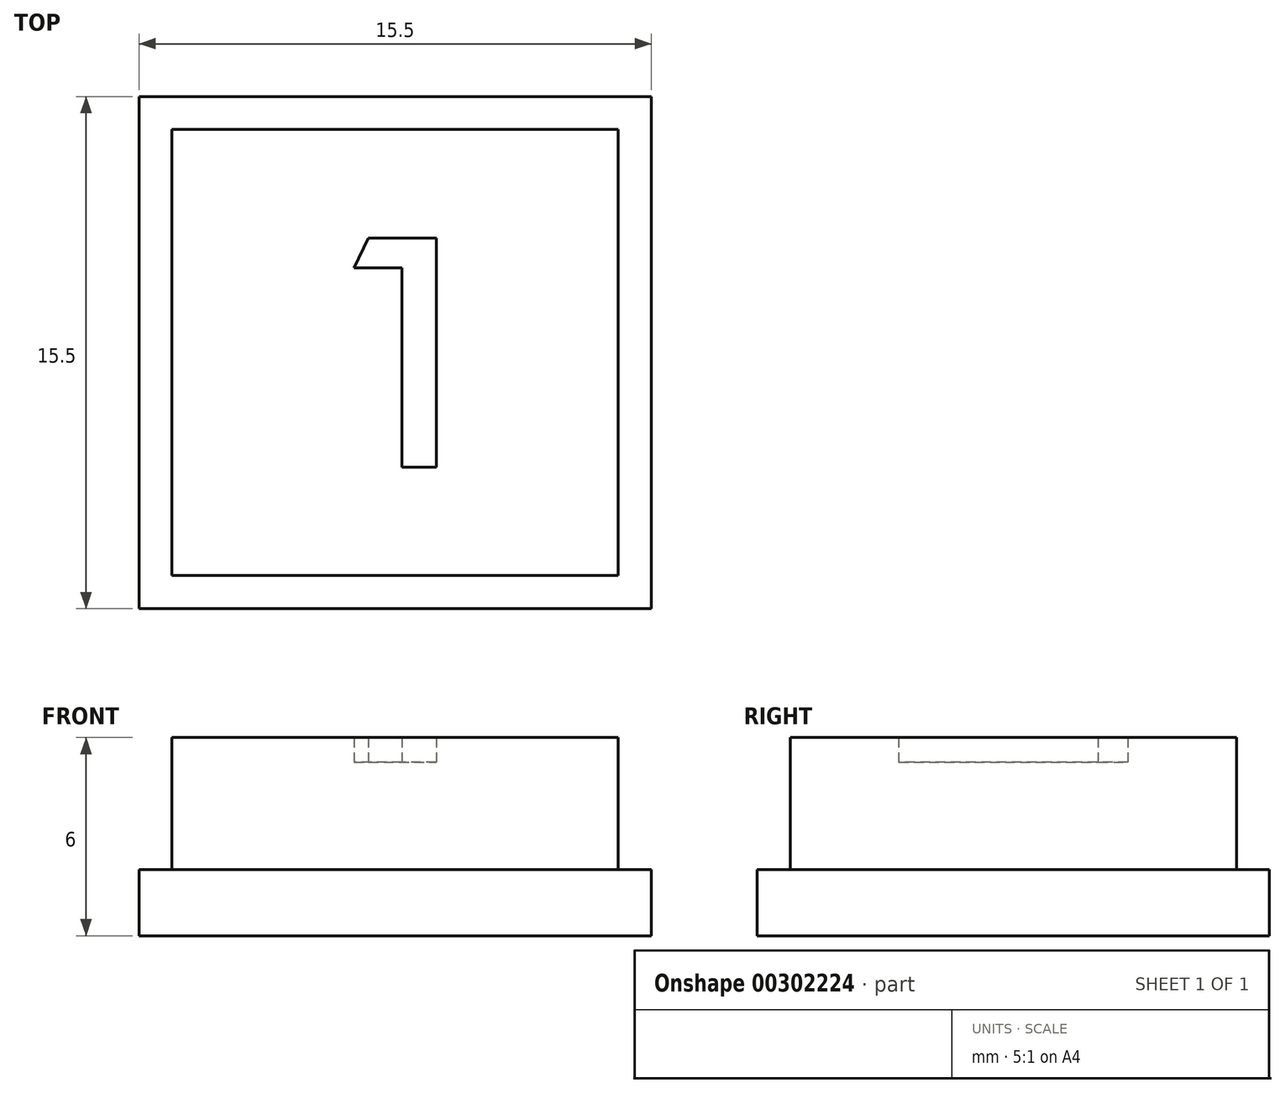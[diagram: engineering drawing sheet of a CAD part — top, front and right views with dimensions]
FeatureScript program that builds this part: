
annotation { "Feature Type Name" : "Feature", "Feature Type Description" : "" }
export const myFeature = defineFeature(function(context is Context, id is Id, definition is map)
    precondition{}
    {
        {
            var Q0;
            Q0=qCreatedBy(makeId("Top.planeOp"),FACE);
            var sketch = newSketch(context, id + "F0", { "sketchPlane" : qUnion([Q0])});
            skLineSegment(sketch, "E0", {"start": v(-6.75, -6.75) * mm, "end": v(6.75, -6.75) * mm});
            skLineSegment(sketch, "E1", {"start": v(6.75, -6.75) * mm, "end": v(6.75, 6.75) * mm});
            skLineSegment(sketch, "E2", {"start": v(6.75, 6.75) * mm, "end": v(-6.75, 6.75) * mm});
            skLineSegment(sketch, "E3", {"start": v(-6.75, 6.75) * mm, "end": v(-6.75, -6.75) * mm});
            skLineSegment(sketch, "E4", {"start": v(-7.75, 7.75) * mm, "end": v(-7.75, -7.75) * mm});
            skLineSegment(sketch, "E5", {"start": v(-7.75, -7.75) * mm, "end": v(7.75, -7.75) * mm});
            skLineSegment(sketch, "E6", {"start": v(7.75, -7.75) * mm, "end": v(7.75, 7.75) * mm});
            skLineSegment(sketch, "E7", {"start": v(7.75, 7.75) * mm, "end": v(-7.75, 7.75) * mm});
            skLineSegment(sketch, "E8", {"start": v(0.2, -3.47) * mm, "end": v(0.2, 2.57) * mm});
            skLineSegment(sketch, "E9", {"start": v(0.2, 2.57) * mm, "end": v(-1.24, 2.57) * mm});
            skLineSegment(sketch, "E10", {"start": v(-1.24, 2.57) * mm, "end": v(-0.8, 3.47) * mm});
            skLineSegment(sketch, "E11", {"start": v(-0.8, 3.47) * mm, "end": v(1.24, 3.47) * mm});
            skLineSegment(sketch, "E12", {"start": v(1.24, 3.47) * mm, "end": v(1.24, -3.47) * mm});
            skLineSegment(sketch, "E13", {"start": v(1.24, -3.47) * mm, "end": v(0.2, -3.47) * mm});
            skSolve(sketch);
        }
        {
            var Q0;
            Q0=makeQuery(id+"F0.imprint","IMPRINT",FACE,{"disambiguationData":[TD([[makeQuery(id+"F0.imprint","IMPRINT",EDGE,{"derivedFrom":sQuery(id+"F0.wireOp",EDGE,"E0")}),-1.0]])]});
            extrude(context, id + "F1", {"entities" : qUnion([Q0]), "depth" : 2 * mm});
        }
        {
            var Q0;
            Q0=makeQuery(id+"F0.imprint","IMPRINT",FACE,{"disambiguationData":[TD([[makeQuery(id+"F0.imprint","IMPRINT",EDGE,{"derivedFrom":sQuery(id+"F0.wireOp",EDGE,"E0")}),1.0]])]});
            extrude(context, id + "F2", {"entities" : qUnion([Q0]), "operationType" : NewBodyOperationType.ADD, "depth" : 6 * mm});
        }
        {
            var Q0;
            Q0=makeQuery(id+"F0.imprint","IMPRINT",FACE,{"disambiguationData":[TD([[makeQuery(id+"F0.imprint","IMPRINT",EDGE,{"derivedFrom":sQuery(id+"F0.wireOp",EDGE,"E8")}),-1.0]])]});
            extrude(context, id + "F3", {"entities" : qUnion([Q0]), "operationType" : NewBodyOperationType.ADD, "depth" : 5.25 * mm});
        }
    });
